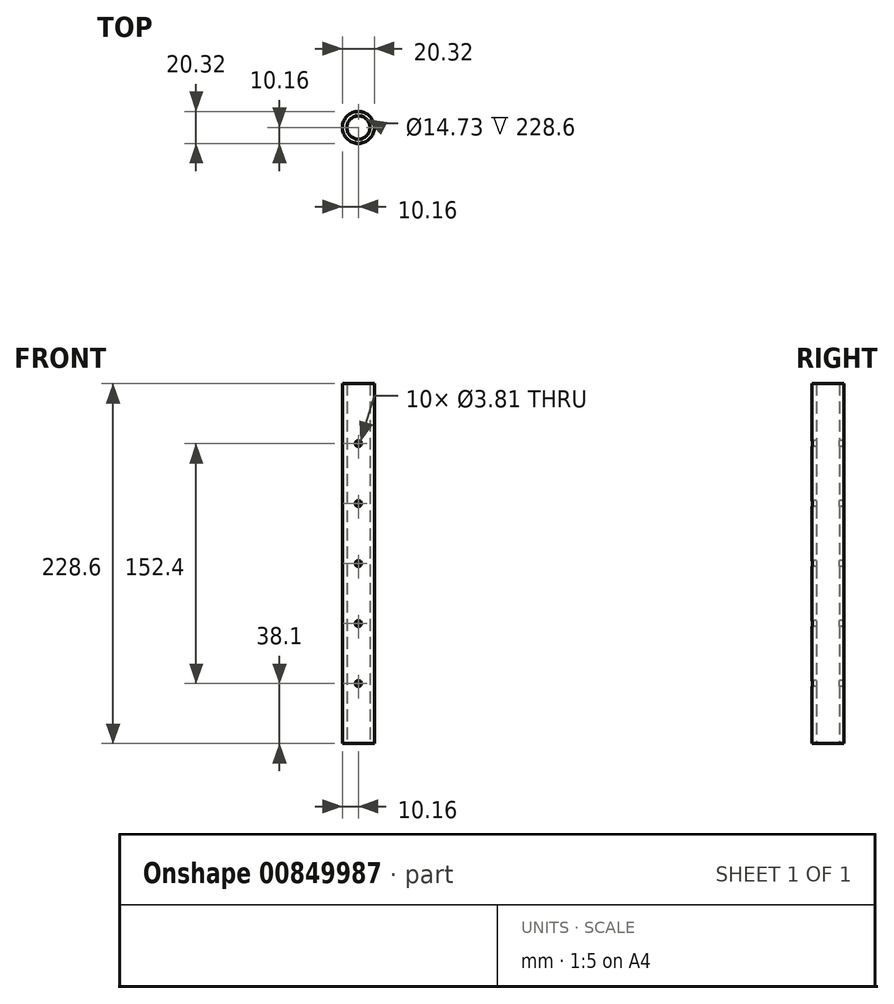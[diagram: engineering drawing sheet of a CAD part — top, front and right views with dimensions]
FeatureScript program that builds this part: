
annotation { "Feature Type Name" : "Feature", "Feature Type Description" : "" }
export const myFeature = defineFeature(function(context is Context, id is Id, definition is map)
    precondition{}
    {
        {
            var Q0;
            Q0=qCreatedBy(makeId("Top.planeOp"),FACE);
            var sketch = newSketch(context, id + "F0", { "sketchPlane" : qUnion([Q0])});
            skCircle(sketch, "E0", {"center": v(0, 0) * mm, "radius": 7.37 * mm});
            skCircle(sketch, "E1", {"center": v(0, 0) * mm, "radius": 10.16 * mm});
            skSolve(sketch);
        }
        {
            var Q0;
            Q0 = qSketchRegion(id + "F0", true);
            extrude(context, id + "F1", {"entities" : qUnion([Q0]), "depth" : 228.6 * mm, "offsetDistance" : 25.4 * mm});
        }
        {
            var Q0;
            Q0=qCreatedBy(makeId("Front.planeOp"),FACE);
            var sketch = newSketch(context, id + "F2", { "sketchPlane" : qUnion([Q0])});
            skCircle(sketch, "E2", {"center": v(0, 38.1) * mm, "radius": 1.9 * mm});
            skCircle(sketch, "E3.0.1.0", {"center": v(0, 76.2) * mm, "radius": 1.9 * mm});
            skCircle(sketch, "E3.0.2.0", {"center": v(0, 114.3) * mm, "radius": 1.9 * mm});
            skCircle(sketch, "E3.0.3.0", {"center": v(0, 152.4) * mm, "radius": 1.9 * mm});
            skCircle(sketch, "E3.0.4.0", {"center": v(0, 190.5) * mm, "radius": 1.9 * mm});
            skLineSegment(sketch, "E3.direction1", {"start": v(0, 38.1) * mm, "end": v(25.4, 38.1) * mm, "construction": true});
            skLineSegment(sketch, "E3.direction2", {"start": v(0, 38.1) * mm, "end": v(0, 76.2) * mm, "construction": true});
            skSolve(sketch);
        }
        {
            var Q0;
            Q0 = qSketchRegion(id + "F2", true);
            extrude(context, id + "F3", {"entities" : qUnion([Q0]), "operationType" : NewBodyOperationType.REMOVE, "oppositeDirection" : true, "depth" : 25.4 * mm, "offsetDistance" : 25.4 * mm, "hasSecondDirection" : true, "secondDirectionOppositeDirection" : false, "secondDirectionDepth" : 25.4 * mm});
        }
    });
